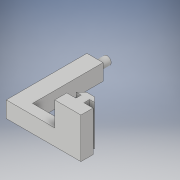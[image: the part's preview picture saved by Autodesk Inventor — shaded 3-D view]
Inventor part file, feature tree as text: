
AUTODESK INVENTOR PART (.ipt)
format: ipt  version: 2018 (Build 220112000, 112)  size: 143,872 bytes
history: native  units: in
note: dims shown in document units (in); Inventor stores cm internally (conversion verified against a paired STEP export)
features: sketch x5, extrude x4, hole x1
ambient origin geometry x8: Origin, YZ Plane, XZ Plane, XY Plane, X Axis, Y Axis, Z Axis, Center Point
bodies: Solid1 (feature_tree)
feature tree (10):
  extrude  "Extrusion1"  Depth=0.3in
  extrude  "Extrusion2"  Depth=0.26in
  extrude  "Extrusion3"  Depth=0.12in
  extrude  "Extrusion4"  Depth=0.12in
  hole  "Hole1"  [1 undecoded]
  sketch  "Sketch1"  dims[d0=0.65in d1=0.3in]
  sketch  "Sketch3"  dims[d2=0.225in d3=0.26in]
  sketch  "Sketch4"  dims[d4=0.2in d5=0.12in]
  sketch  "Sketch5"  dims[d6=0.12in d7=0.12in]
  sketch  "Sketch6"  dims[d8=1.0in d9=0.0in d10=0.25in d11=0.4in d12=1.2in d13=0.0in d14=0.4in d15=0.4in d16=1.75in d17=0.0in d18=0.2in d19=0.2in d20=0.3in d21=0.0in d22=0.11in d23=0.75in d24=0.375in d25=0.25in d26=0.5635in d27=0.63in d28=0.8108in]
note: 1 required parameter value undecoded (feature->parameter linkage not recoverable at this tier; creation-order binding heuristic only, values carry confidence <= 0.55)
